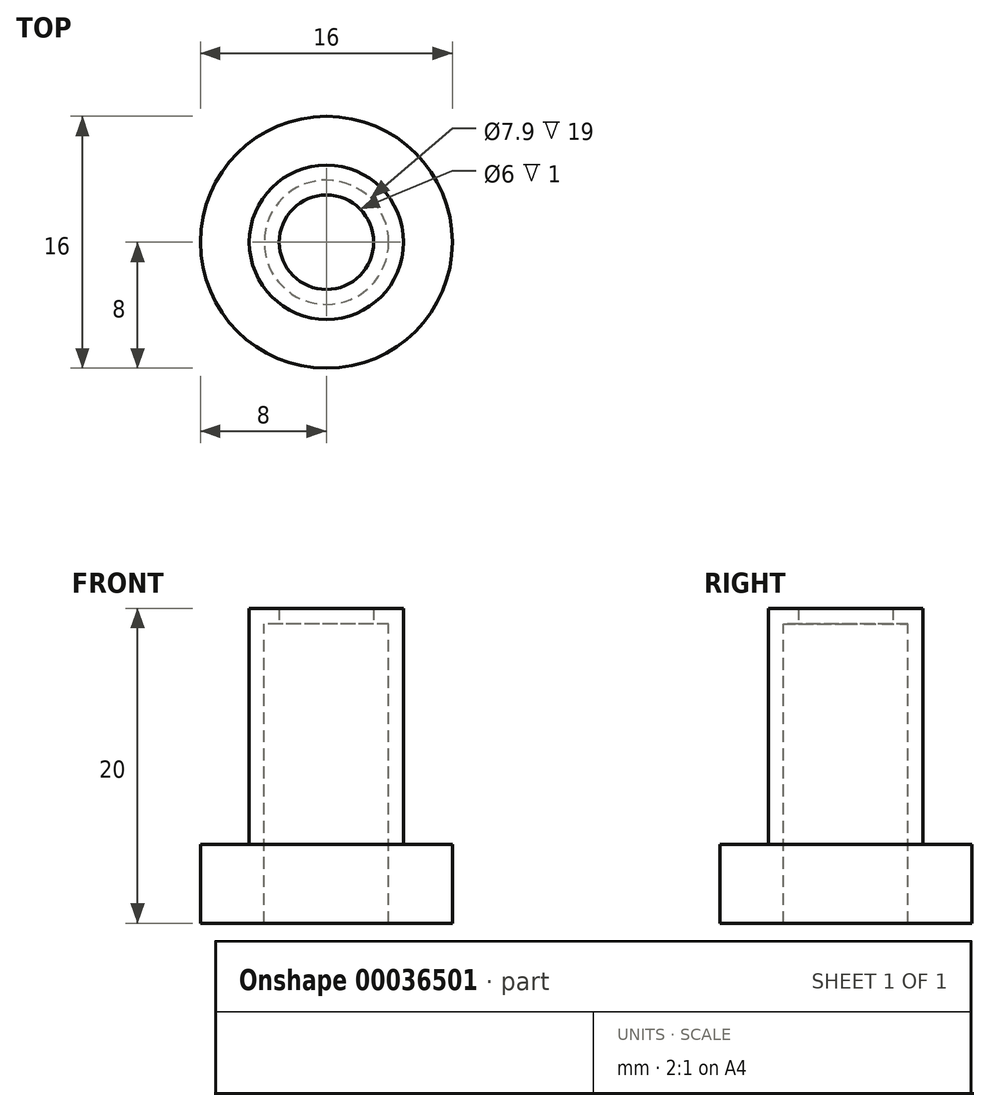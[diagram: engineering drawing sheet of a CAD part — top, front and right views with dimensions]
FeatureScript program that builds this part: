
annotation { "Feature Type Name" : "Feature", "Feature Type Description" : "" }
export const myFeature = defineFeature(function(context is Context, id is Id, definition is map)
    precondition{}
    {
        {
            var Q0;
            Q0=qCreatedBy(makeId("Top.planeOp"),FACE);
            var sketch = newSketch(context, id + "F0", { "sketchPlane" : qUnion([Q0])});
            skCircle(sketch, "E0", {"center": v(0, 0) * mm, "radius": 4.9 * mm});
            skSolve(sketch);
        }
        {
            var Q0;
            Q0 = qSketchRegion(id + "F0", true);
            extrude(context, id + "F1", {"entities" : qUnion([Q0]), "depth" : 14 * mm, "offsetDistance" : 25 * mm});
        }
        {
            var Q0;
            Q0=qCreatedBy(makeId("Top.planeOp"),FACE);
            var sketch = newSketch(context, id + "F2", { "sketchPlane" : qUnion([Q0])});
            skCircle(sketch, "E1", {"center": v(0, 0) * mm, "radius": 8 * mm});
            skSolve(sketch);
        }
        {
            var Q0;
            Q0 = qSketchRegion(id + "F2", true);
            extrude(context, id + "F3", {"entities" : qUnion([Q0]), "operationType" : NewBodyOperationType.ADD, "oppositeDirection" : true, "depth" : 5 * mm, "offsetDistance" : 25 * mm});
        }
        {
            var Q0;
            Q0=qCreatedBy(makeId("Top.planeOp"),FACE);
            var sketch = newSketch(context, id + "F4", { "sketchPlane" : qUnion([Q0])});
            skCircle(sketch, "E2", {"center": v(0, 0) * mm, "radius": 3.95 * mm});
            skSolve(sketch);
        }
        {
            var Q0;
            Q0 = qSketchRegion(id + "F4", true);
            extrude(context, id + "F5", {"entities" : qUnion([Q0]), "operationType" : NewBodyOperationType.REMOVE, "oppositeDirection" : true, "depth" : 25 * mm, "offsetDistance" : 25 * mm, "hasSecondDirection" : true, "secondDirectionOppositeDirection" : false, "secondDirectionDepth" : 25 * mm});
        }
        {
            var Q0;
            Q0=qCreatedBy(makeId("Top.planeOp"),FACE);
            cPlane(context, id + "F6", {"entities" : qUnion([Q0]), "cplaneType" : CPlaneType.OFFSET, "offset" : 14 * mm, "width" : 150 * mm, "height" : 150 * mm});
        }
        {
            var Q0;
            Q0=qCreatedBy(id+"F6.planeOp",FACE);
            var sketch = newSketch(context, id + "F7", { "sketchPlane" : qUnion([Q0])});
            skCircle(sketch, "E3", {"center": v(0, 0) * mm, "radius": 3 * mm});
            skCircle(sketch, "E4", {"center": v(0, 0) * mm, "radius": 4.9 * mm});
            skSolve(sketch);
        }
        {
            var Q0;
            Q0 = qSketchRegion(id + "F7", true);
            extrude(context, id + "F8", {"entities" : qUnion([Q0]), "operationType" : NewBodyOperationType.ADD, "depth" : 1 * mm, "offsetDistance" : 25 * mm});
        }
    });
